# Revit family: QF_Summit_EL51LT_Chest_Freezer
name_source: partatom
category: Specialty Equipment
units: mm (PartAtom-declared; Revit-internal decimal feet)

## family parameters
Always vertical = Yes
Cut with Voids When Loaded = No
Part Type = Normal
Room Calculation Point = No
Round Connector Dimension = Use Diameter
Shared = No
Work Plane-Based = No

## types (1)
- QF_Summit_EL51LT_Chest_Freezer
    Apparent Power = 0 VA
    BTUH = 0.0 Btu/h
    Conn Conduit = Yes
    Cycle = 60 Hz
    Default Elevation = 0"
    Depth = 27 1/4"
    Description = Chest Freezer
    Elec Conn Connection Height = 0"
    Elec Conn RI Height = 0"
    FL Amps = 7 A
    Foodservice Equipment Identifier = Yes
    Height = 33 1/2"
    Identify Quantity as Lot = Yes
    Length = 67"
    Manufacturer = Summit
    Max Overcurrent Protection = 0 A
    Min Ckt Ampacity = 0 A
    Model = EL51LT
    Number of Poles = 1
    Phase = 1
    Refrigerant Type = R920a
    Refrigerant Volume = 0.00 kip
    Volts = 115 V
    Watts = 817 W
    Weight in Pounds = 210

## geometry (parser evidence)
native form markers: Sweep x9
no freeform markers — native parametric forms only
